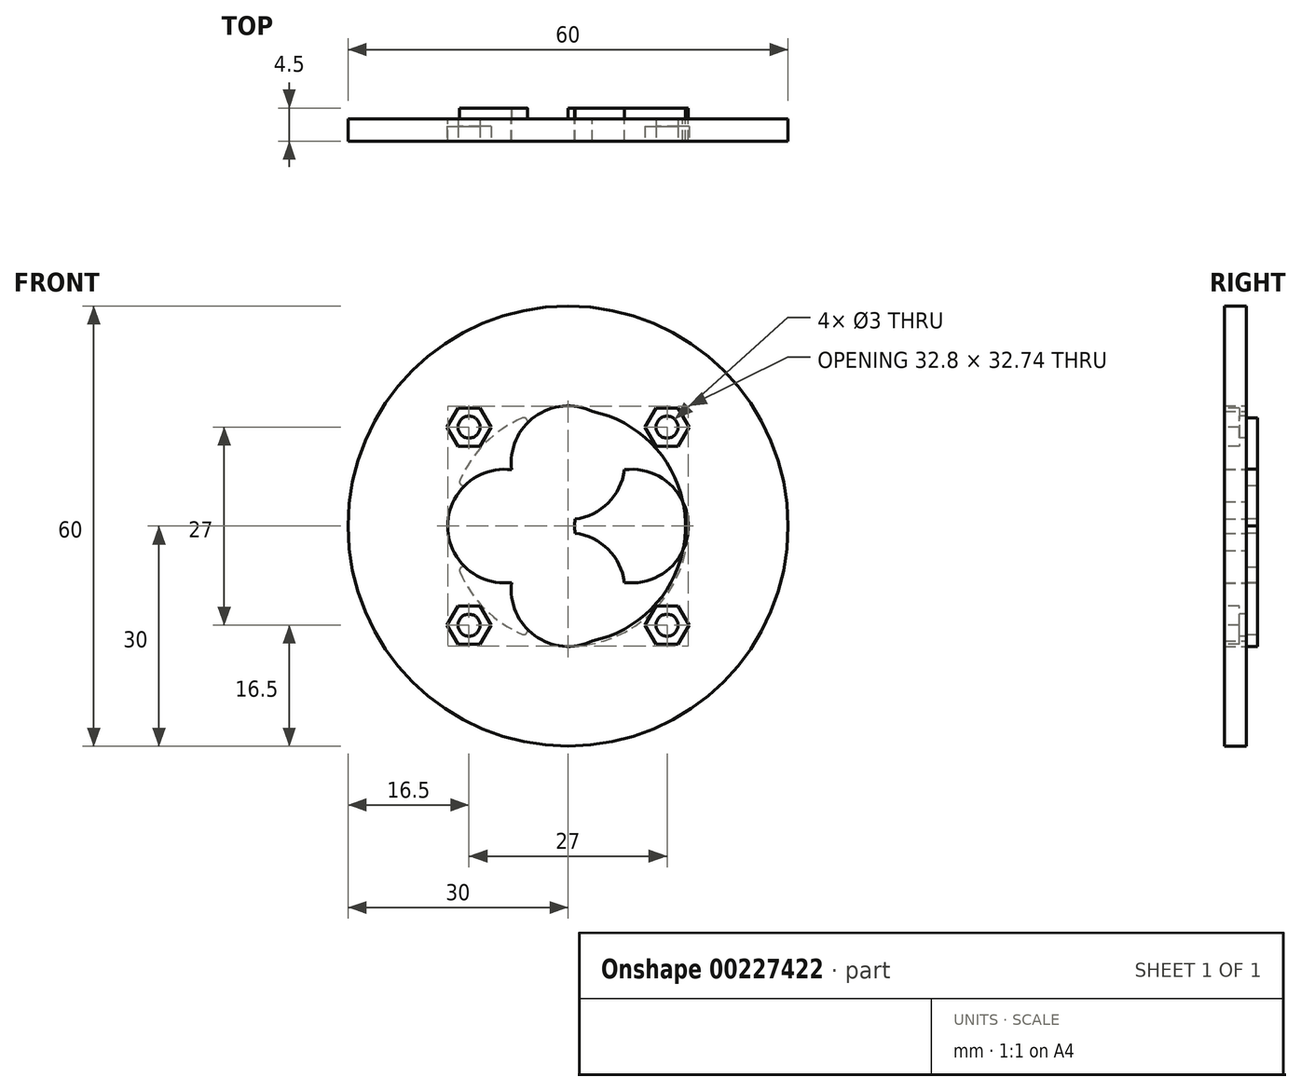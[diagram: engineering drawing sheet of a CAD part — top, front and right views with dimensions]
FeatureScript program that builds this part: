
annotation { "Feature Type Name" : "Feature", "Feature Type Description" : "" }
export const myFeature = defineFeature(function(context is Context, id is Id, definition is map)
    precondition{}
    {
        {
            var Q0;
            Q0=qCreatedBy(makeId("Front.planeOp"),FACE);
            var sketch = newSketch(context, id + "F0", { "sketchPlane" : qUnion([Q0])});
            skCircle(sketch, "E0", {"center": v(0, 0) * mm, "radius": 16.4 * mm});
            skCircle(sketch, "E1", {"center": v(0, -8.65) * mm, "radius": 7.75 * mm});
            skCircle(sketch, "E2", {"center": v(8.65, 0) * mm, "radius": 7.75 * mm});
            skCircle(sketch, "E3", {"center": v(0, 8.65) * mm, "radius": 7.75 * mm});
            skCircle(sketch, "E4", {"center": v(-8.65, 0) * mm, "radius": 7.75 * mm});
            skCircle(sketch, "E5", {"center": v(0, 0) * mm, "radius": 30 * mm});
            skCircle(sketch, "E6", {"center": v(0, 0) * mm, "radius": 16 * mm});
            skSolve(sketch);
        }
        {
            var Q0;
            Q0=makeQuery(id+"F0.imprint","IMPRINT",FACE,{"disambiguationData":[TD([[makeQuery(id+"F0.imprint","IMPRINT",EDGE,{"derivedFrom":sQuery(id+"F0.wireOp",EDGE,"E5")}),1.0]])]});
            var Q1;
            {var subQ0=sQuery(id+"F0.wireOp",EDGE,"E3");var subQ1=sQuery(id+"F0.wireOp",EDGE,"E0");var subQ2=makeQuery(id+"F0.imprint","INTERSECT",VERTEX,{"derivedFrom":[subQ1,subQ0]});Q1=makeQuery(id+"F0.imprint","IMPRINT",FACE,{"disambiguationData":[TD([[makeQuery(id+"F0.imprint","IMPRINT",EDGE,{"disambiguationData":[TD([[subQ2,-1.0]])],"derivedFrom":subQ1}),1.0]])]});}
            var Q2;
            {var subQ0=sQuery(id+"F0.wireOp",EDGE,"E6");var subQ1=sQuery(id+"F0.wireOp",EDGE,"E3");var subQ2=makeQuery(id+"F0.imprint","INTERSECT",VERTEX,{"disambiguationData":[OD(1.0)],"derivedFrom":[subQ1,subQ0]});Q2=makeQuery(id+"F0.imprint","IMPRINT",FACE,{"disambiguationData":[TD([[makeQuery(id+"F0.imprint","IMPRINT",EDGE,{"disambiguationData":[TD([[subQ2,-1.0]])],"derivedFrom":subQ1}),-1.0]])]});}
            var Q3;
            {var subQ0=sQuery(id+"F0.wireOp",EDGE,"E4");var subQ1=sQuery(id+"F0.wireOp",EDGE,"E0");var subQ2=makeQuery(id+"F0.imprint","INTERSECT",VERTEX,{"derivedFrom":[subQ1,subQ0]});Q3=makeQuery(id+"F0.imprint","IMPRINT",FACE,{"disambiguationData":[TD([[makeQuery(id+"F0.imprint","IMPRINT",EDGE,{"disambiguationData":[TD([[subQ2,-1.0]])],"derivedFrom":subQ1}),1.0]])]});}
            var Q4;
            {var subQ0=sQuery(id+"F0.wireOp",EDGE,"E4");var subQ1=sQuery(id+"F0.wireOp",EDGE,"E1");var subQ2=makeQuery(id+"F0.imprint","INTERSECT",VERTEX,{"disambiguationData":[OD(1.0)],"derivedFrom":[subQ1,subQ0]});Q4=makeQuery(id+"F0.imprint","IMPRINT",FACE,{"disambiguationData":[TD([[makeQuery(id+"F0.imprint","IMPRINT",EDGE,{"disambiguationData":[TD([[subQ2,-1.0]])],"derivedFrom":subQ1}),-1.0]])]});}
            var Q5;
            {var subQ0=sQuery(id+"F0.wireOp",EDGE,"E3");var subQ1=sQuery(id+"F0.wireOp",EDGE,"E0");var subQ2=makeQuery(id+"F0.imprint","INTERSECT",VERTEX,{"derivedFrom":[subQ1,subQ0]});Q5=makeQuery(id+"F0.imprint","IMPRINT",FACE,{"disambiguationData":[TD([[makeQuery(id+"F0.imprint","IMPRINT",EDGE,{"disambiguationData":[TD([[subQ2,1.0]])],"derivedFrom":subQ1}),1.0]])]});}
            var Q6;
            {var subQ0=sQuery(id+"F0.wireOp",EDGE,"E6");var subQ1=sQuery(id+"F0.wireOp",EDGE,"E2");var subQ2=makeQuery(id+"F0.imprint","INTERSECT",VERTEX,{"disambiguationData":[OD(0.0)],"derivedFrom":[subQ1,subQ0]});Q6=makeQuery(id+"F0.imprint","IMPRINT",FACE,{"disambiguationData":[TD([[makeQuery(id+"F0.imprint","IMPRINT",EDGE,{"disambiguationData":[TD([[subQ2,-1.0]])],"derivedFrom":subQ1}),-1.0]])]});}
            var Q7;
            {var subQ0=sQuery(id+"F0.wireOp",EDGE,"E2");var subQ1=sQuery(id+"F0.wireOp",EDGE,"E0");var subQ2=makeQuery(id+"F0.imprint","INTERSECT",VERTEX,{"derivedFrom":[subQ1,subQ0]});Q7=makeQuery(id+"F0.imprint","IMPRINT",FACE,{"disambiguationData":[TD([[makeQuery(id+"F0.imprint","IMPRINT",EDGE,{"disambiguationData":[TD([[subQ2,1.0]])],"derivedFrom":subQ1}),1.0]])]});}
            var Q8;
            {var subQ0=sQuery(id+"F0.wireOp",EDGE,"E2");var subQ1=sQuery(id+"F0.wireOp",EDGE,"E1");var subQ2=makeQuery(id+"F0.imprint","INTERSECT",VERTEX,{"disambiguationData":[OD(1.0)],"derivedFrom":[subQ1,subQ0]});Q8=makeQuery(id+"F0.imprint","IMPRINT",FACE,{"disambiguationData":[TD([[makeQuery(id+"F0.imprint","IMPRINT",EDGE,{"disambiguationData":[TD([[subQ2,1.0]])],"derivedFrom":subQ1}),-1.0]])]});}
            extrude(context, id + "F1", {"entities" : qUnion([Q0, Q1, Q2, Q3, Q4, Q5, Q6, Q7, Q8]), "depth" : 3 * mm});
        }
        {
            var Q0;
            {var subQ0=sQuery(id+"F0.wireOp",EDGE,"E6");var subQ1=sQuery(id+"F0.wireOp",EDGE,"E2");var subQ2=makeQuery(id+"F0.imprint","INTERSECT",VERTEX,{"disambiguationData":[OD(0.0)],"derivedFrom":[subQ1,subQ0]});Q0=makeQuery(id+"F0.imprint","IMPRINT",FACE,{"disambiguationData":[TD([[makeQuery(id+"F0.imprint","IMPRINT",EDGE,{"disambiguationData":[TD([[subQ2,-1.0]])],"derivedFrom":subQ1}),-1.0]])]});}
            var Q1;
            {var subQ0=sQuery(id+"F0.wireOp",EDGE,"E2");var subQ1=sQuery(id+"F0.wireOp",EDGE,"E1");var subQ2=makeQuery(id+"F0.imprint","INTERSECT",VERTEX,{"disambiguationData":[OD(1.0)],"derivedFrom":[subQ1,subQ0]});Q1=makeQuery(id+"F0.imprint","IMPRINT",FACE,{"disambiguationData":[TD([[makeQuery(id+"F0.imprint","IMPRINT",EDGE,{"disambiguationData":[TD([[subQ2,1.0]])],"derivedFrom":subQ1}),-1.0]])]});}
            var Q2;
            {var subQ0=sQuery(id+"F0.wireOp",EDGE,"E4");var subQ1=sQuery(id+"F0.wireOp",EDGE,"E1");var subQ2=makeQuery(id+"F0.imprint","INTERSECT",VERTEX,{"disambiguationData":[OD(1.0)],"derivedFrom":[subQ1,subQ0]});Q2=makeQuery(id+"F0.imprint","IMPRINT",FACE,{"disambiguationData":[TD([[makeQuery(id+"F0.imprint","IMPRINT",EDGE,{"disambiguationData":[TD([[subQ2,-1.0]])],"derivedFrom":subQ1}),-1.0]])]});}
            var Q3;
            {var subQ0=sQuery(id+"F0.wireOp",EDGE,"E6");var subQ1=sQuery(id+"F0.wireOp",EDGE,"E3");var subQ2=makeQuery(id+"F0.imprint","INTERSECT",VERTEX,{"disambiguationData":[OD(1.0)],"derivedFrom":[subQ1,subQ0]});Q3=makeQuery(id+"F0.imprint","IMPRINT",FACE,{"disambiguationData":[TD([[makeQuery(id+"F0.imprint","IMPRINT",EDGE,{"disambiguationData":[TD([[subQ2,-1.0]])],"derivedFrom":subQ1}),-1.0]])]});}
            extrude(context, id + "F4", {"entities" : qUnion([Q0, Q1, Q2, Q3]), "oppositeDirection" : true, "depth" : 1.5 * mm});
        }
        {
            var Q0;
            {var subQ0=sQuery(id+"F0.wireOp",EDGE,"E6");var subQ1=sQuery(id+"F0.wireOp",EDGE,"E1");Q0=makeQuery(id+"F4.opExtrude","SWEPT_EDGE",EDGE,{"disambiguationData":[OSD([subQ1,subQ0]),TDD([makeQuery(id+"F0.imprint","INTERSECT",VERTEX,{"disambiguationData":[OD(0.0)],"derivedFrom":[subQ1,subQ0]})])]});}
            var Q1;
            {var subQ0=sQuery(id+"F0.wireOp",EDGE,"E6");var subQ1=sQuery(id+"F0.wireOp",EDGE,"E1");Q1=makeQuery(id+"F4.opExtrude","SWEPT_EDGE",EDGE,{"disambiguationData":[OSD([subQ1,subQ0]),TDD([makeQuery(id+"F0.imprint","INTERSECT",VERTEX,{"disambiguationData":[OD(1.0)],"derivedFrom":[subQ1,subQ0]})])]});}
            var Q2;
            {var subQ0=sQuery(id+"F0.wireOp",EDGE,"E6");var subQ1=sQuery(id+"F0.wireOp",EDGE,"E2");Q2=makeQuery(id+"F4.opExtrude","SWEPT_EDGE",EDGE,{"disambiguationData":[OSD([subQ1,subQ0]),TDD([makeQuery(id+"F0.imprint","INTERSECT",VERTEX,{"disambiguationData":[OD(0.0)],"derivedFrom":[subQ1,subQ0]})])]});}
            var Q3;
            {var subQ0=sQuery(id+"F0.wireOp",EDGE,"E6");var subQ1=sQuery(id+"F0.wireOp",EDGE,"E2");Q3=makeQuery(id+"F4.opExtrude","SWEPT_EDGE",EDGE,{"disambiguationData":[OSD([subQ1,subQ0]),TDD([makeQuery(id+"F0.imprint","INTERSECT",VERTEX,{"disambiguationData":[OD(1.0)],"derivedFrom":[subQ1,subQ0]})])]});}
            var Q4;
            {var subQ0=sQuery(id+"F0.wireOp",EDGE,"E6");var subQ1=sQuery(id+"F0.wireOp",EDGE,"E2");Q4=makeQuery(id+"F4.opExtrude","SWEPT_EDGE",EDGE,{"disambiguationData":[OSD([subQ1,subQ0]),TDD([makeQuery(id+"F0.imprint","INTERSECT",VERTEX,{"disambiguationData":[OD(0.0)],"derivedFrom":[subQ1,subQ0]})])]});}
            var Q5;
            {var subQ0=sQuery(id+"F0.wireOp",EDGE,"E6");var subQ1=sQuery(id+"F0.wireOp",EDGE,"E2");Q5=makeQuery(id+"F4.opExtrude","SWEPT_EDGE",EDGE,{"disambiguationData":[OSD([subQ1,subQ0]),TDD([makeQuery(id+"F0.imprint","INTERSECT",VERTEX,{"disambiguationData":[OD(1.0)],"derivedFrom":[subQ1,subQ0]})])]});}
            var Q6;
            {var subQ0=sQuery(id+"F0.wireOp",EDGE,"E6");var subQ1=sQuery(id+"F0.wireOp",EDGE,"E1");Q6=makeQuery(id+"F4.opExtrude","SWEPT_EDGE",EDGE,{"disambiguationData":[OSD([subQ1,subQ0]),TDD([makeQuery(id+"F0.imprint","INTERSECT",VERTEX,{"disambiguationData":[OD(0.0)],"derivedFrom":[subQ1,subQ0]})])]});}
            var Q7;
            {var subQ0=sQuery(id+"F0.wireOp",EDGE,"E6");var subQ1=sQuery(id+"F0.wireOp",EDGE,"E1");Q7=makeQuery(id+"F4.opExtrude","SWEPT_EDGE",EDGE,{"disambiguationData":[OSD([subQ1,subQ0]),TDD([makeQuery(id+"F0.imprint","INTERSECT",VERTEX,{"disambiguationData":[OD(1.0)],"derivedFrom":[subQ1,subQ0]})])]});}
            var Q8;
            {var subQ0=sQuery(id+"F0.wireOp",EDGE,"E6");var subQ1=sQuery(id+"F0.wireOp",EDGE,"E4");Q8=makeQuery(id+"F4.opExtrude","SWEPT_EDGE",EDGE,{"disambiguationData":[OSD([subQ1,subQ0]),TDD([makeQuery(id+"F0.imprint","INTERSECT",VERTEX,{"disambiguationData":[OD(0.0)],"derivedFrom":[subQ1,subQ0]})])]});}
            var Q9;
            {var subQ0=sQuery(id+"F0.wireOp",EDGE,"E6");var subQ1=sQuery(id+"F0.wireOp",EDGE,"E4");Q9=makeQuery(id+"F4.opExtrude","SWEPT_EDGE",EDGE,{"disambiguationData":[OSD([subQ1,subQ0]),TDD([makeQuery(id+"F0.imprint","INTERSECT",VERTEX,{"disambiguationData":[OD(1.0)],"derivedFrom":[subQ1,subQ0]})])]});}
            var Q10;
            {var subQ0=sQuery(id+"F0.wireOp",EDGE,"E6");var subQ1=sQuery(id+"F0.wireOp",EDGE,"E3");Q10=makeQuery(id+"F4.opExtrude","SWEPT_EDGE",EDGE,{"disambiguationData":[OSD([subQ1,subQ0]),TDD([makeQuery(id+"F0.imprint","INTERSECT",VERTEX,{"disambiguationData":[OD(0.0)],"derivedFrom":[subQ1,subQ0]})])]});}
            var Q11;
            {var subQ0=sQuery(id+"F0.wireOp",EDGE,"E6");var subQ1=sQuery(id+"F0.wireOp",EDGE,"E3");Q11=makeQuery(id+"F4.opExtrude","SWEPT_EDGE",EDGE,{"disambiguationData":[OSD([subQ1,subQ0]),TDD([makeQuery(id+"F0.imprint","INTERSECT",VERTEX,{"disambiguationData":[OD(1.0)],"derivedFrom":[subQ1,subQ0]})])]});}
            var Q12;
            {var subQ0=sQuery(id+"F0.wireOp",EDGE,"E6");var subQ1=sQuery(id+"F0.wireOp",EDGE,"E1");Q12=makeQuery(id+"F4.opExtrude","SWEPT_EDGE",EDGE,{"disambiguationData":[OSD([subQ1,subQ0]),TDD([makeQuery(id+"F0.imprint","INTERSECT",VERTEX,{"disambiguationData":[OD(0.0)],"derivedFrom":[subQ1,subQ0]})])]});}
            var Q13;
            {var subQ0=sQuery(id+"F0.wireOp",EDGE,"E6");var subQ1=sQuery(id+"F0.wireOp",EDGE,"E1");Q13=makeQuery(id+"F4.opExtrude","SWEPT_EDGE",EDGE,{"disambiguationData":[OSD([subQ1,subQ0]),TDD([makeQuery(id+"F0.imprint","INTERSECT",VERTEX,{"disambiguationData":[OD(1.0)],"derivedFrom":[subQ1,subQ0]})])]});}
            var Q14;
            {var subQ0=sQuery(id+"F0.wireOp",EDGE,"E6");var subQ1=sQuery(id+"F0.wireOp",EDGE,"E2");Q14=makeQuery(id+"F4.opExtrude","SWEPT_EDGE",EDGE,{"disambiguationData":[OSD([subQ1,subQ0]),TDD([makeQuery(id+"F0.imprint","INTERSECT",VERTEX,{"disambiguationData":[OD(0.0)],"derivedFrom":[subQ1,subQ0]})])]});}
            var Q15;
            {var subQ0=sQuery(id+"F0.wireOp",EDGE,"E6");var subQ1=sQuery(id+"F0.wireOp",EDGE,"E2");Q15=makeQuery(id+"F4.opExtrude","SWEPT_EDGE",EDGE,{"disambiguationData":[OSD([subQ1,subQ0]),TDD([makeQuery(id+"F0.imprint","INTERSECT",VERTEX,{"disambiguationData":[OD(1.0)],"derivedFrom":[subQ1,subQ0]})])]});}
            var Q16;
            {var subQ0=sQuery(id+"F0.wireOp",EDGE,"E6");var subQ1=sQuery(id+"F0.wireOp",EDGE,"E4");Q16=makeQuery(id+"F4.opExtrude","SWEPT_EDGE",EDGE,{"disambiguationData":[OSD([subQ1,subQ0]),TDD([makeQuery(id+"F0.imprint","INTERSECT",VERTEX,{"disambiguationData":[OD(0.0)],"derivedFrom":[subQ1,subQ0]})])]});}
            var Q17;
            {var subQ0=sQuery(id+"F0.wireOp",EDGE,"E6");var subQ1=sQuery(id+"F0.wireOp",EDGE,"E4");Q17=makeQuery(id+"F4.opExtrude","SWEPT_EDGE",EDGE,{"disambiguationData":[OSD([subQ1,subQ0]),TDD([makeQuery(id+"F0.imprint","INTERSECT",VERTEX,{"disambiguationData":[OD(1.0)],"derivedFrom":[subQ1,subQ0]})])]});}
            var Q18;
            {var subQ0=sQuery(id+"F0.wireOp",EDGE,"E6");var subQ1=sQuery(id+"F0.wireOp",EDGE,"E3");Q18=makeQuery(id+"F4.opExtrude","SWEPT_EDGE",EDGE,{"disambiguationData":[OSD([subQ1,subQ0]),TDD([makeQuery(id+"F0.imprint","INTERSECT",VERTEX,{"disambiguationData":[OD(0.0)],"derivedFrom":[subQ1,subQ0]})])]});}
            var Q19;
            {var subQ0=sQuery(id+"F0.wireOp",EDGE,"E6");var subQ1=sQuery(id+"F0.wireOp",EDGE,"E3");Q19=makeQuery(id+"F4.opExtrude","SWEPT_EDGE",EDGE,{"disambiguationData":[OSD([subQ1,subQ0]),TDD([makeQuery(id+"F0.imprint","INTERSECT",VERTEX,{"disambiguationData":[OD(1.0)],"derivedFrom":[subQ1,subQ0]})])]});}
            var Q20;
            {var subQ0=sQuery(id+"F0.wireOp",EDGE,"E6");var subQ1=sQuery(id+"F0.wireOp",EDGE,"E2");Q20=makeQuery(id+"F4.opExtrude","SWEPT_EDGE",EDGE,{"disambiguationData":[OSD([subQ1,subQ0]),TDD([makeQuery(id+"F0.imprint","INTERSECT",VERTEX,{"disambiguationData":[OD(0.0)],"derivedFrom":[subQ1,subQ0]})])]});}
            var Q21;
            {var subQ0=sQuery(id+"F0.wireOp",EDGE,"E6");var subQ1=sQuery(id+"F0.wireOp",EDGE,"E2");Q21=makeQuery(id+"F4.opExtrude","SWEPT_EDGE",EDGE,{"disambiguationData":[OSD([subQ1,subQ0]),TDD([makeQuery(id+"F0.imprint","INTERSECT",VERTEX,{"disambiguationData":[OD(1.0)],"derivedFrom":[subQ1,subQ0]})])]});}
            fillet(context, id + "F5", {"entities" : qUnion([Q0, Q1, Q2, Q3, Q4, Q5, Q6, Q7, Q8, Q9, Q10, Q11, Q12, Q13, Q14, Q15, Q16, Q17, Q18, Q19, Q20, Q21]), "radius" : 0.5 * mm, "tangentPropagation" : true, "allowEdgeOverflow" : false});
        }
        {
            var Q0;
            Q0=makeQuery(id+"F1.opExtrude","CAP_FACE",FACE,{"disambiguationData":[OSD([sQuery(id+"F0.wireOp",EDGE,"E1"),sQuery(id+"F0.wireOp",EDGE,"E2"),sQuery(id+"F0.wireOp",EDGE,"E3"),sQuery(id+"F0.wireOp",EDGE,"E4"),sQuery(id+"F0.wireOp",EDGE,"E5")])],"isStart":false});
            var sketch = newSketch(context, id + "F2", { "sketchPlane" : qUnion([Q0])});
            skLineSegment(sketch, "E7.bottom", {"start": v(13.5, -13.5) * mm, "end": v(-13.5, -13.5) * mm, "construction": true});
            skLineSegment(sketch, "E7.top", {"start": v(13.5, 13.5) * mm, "end": v(-13.5, 13.5) * mm, "construction": true});
            skLineSegment(sketch, "E7.left", {"start": v(13.5, -13.5) * mm, "end": v(13.5, 13.5) * mm, "construction": true});
            skLineSegment(sketch, "E7.right", {"start": v(-13.5, -13.5) * mm, "end": v(-13.5, 13.5) * mm, "construction": true});
            skPoint(sketch, "E7.middle", {"position": v(0, 0) * mm});
            skCircle(sketch, "E8.cCircle", {"center": v(-13.5, 13.5) * mm, "radius": 2.6 * mm, "construction": true});
            skLineSegment(sketch, "E8.0", {"start": v(-12, 10.9) * mm, "end": v(-15, 10.9) * mm});
            skLineSegment(sketch, "E8.1", {"start": v(-15, 10.9) * mm, "end": v(-16.5, 13.5) * mm});
            skLineSegment(sketch, "E8.2", {"start": v(-16.5, 13.5) * mm, "end": v(-15, 16.1) * mm});
            skLineSegment(sketch, "E8.3", {"start": v(-15, 16.1) * mm, "end": v(-12, 16.1) * mm});
            skLineSegment(sketch, "E8.4", {"start": v(-12, 16.1) * mm, "end": v(-10.5, 13.5) * mm});
            skLineSegment(sketch, "E8.5", {"start": v(-10.5, 13.5) * mm, "end": v(-12, 10.9) * mm});
            skPoint(sketch, "E8.0.midPoint", {"position": v(-13.5, 10.9) * mm});
            skCircle(sketch, "E9.cCircle", {"center": v(13.5, 13.5) * mm, "radius": 2.6 * mm, "construction": true});
            skLineSegment(sketch, "E9.0", {"start": v(15, 10.9) * mm, "end": v(12, 10.9) * mm});
            skLineSegment(sketch, "E9.1", {"start": v(12, 10.9) * mm, "end": v(10.5, 13.5) * mm});
            skLineSegment(sketch, "E9.2", {"start": v(10.5, 13.5) * mm, "end": v(12, 16.1) * mm});
            skLineSegment(sketch, "E9.3", {"start": v(12, 16.1) * mm, "end": v(15, 16.1) * mm});
            skLineSegment(sketch, "E9.4", {"start": v(15, 16.1) * mm, "end": v(16.5, 13.5) * mm});
            skLineSegment(sketch, "E9.5", {"start": v(16.5, 13.5) * mm, "end": v(15, 10.9) * mm});
            skPoint(sketch, "E9.0.midPoint", {"position": v(13.5, 10.9) * mm});
            skCircle(sketch, "E10.cCircle", {"center": v(13.5, -13.5) * mm, "radius": 2.6 * mm, "construction": true});
            skLineSegment(sketch, "E10.0", {"start": v(12, -10.9) * mm, "end": v(15, -10.9) * mm});
            skLineSegment(sketch, "E10.1", {"start": v(15, -10.9) * mm, "end": v(16.5, -13.5) * mm});
            skLineSegment(sketch, "E10.2", {"start": v(16.5, -13.5) * mm, "end": v(15, -16.1) * mm});
            skLineSegment(sketch, "E10.3", {"start": v(15, -16.1) * mm, "end": v(12, -16.1) * mm});
            skLineSegment(sketch, "E10.4", {"start": v(12, -16.1) * mm, "end": v(10.5, -13.5) * mm});
            skLineSegment(sketch, "E10.5", {"start": v(10.5, -13.5) * mm, "end": v(12, -10.9) * mm});
            skPoint(sketch, "E10.0.midPoint", {"position": v(13.5, -10.9) * mm});
            skCircle(sketch, "E11.cCircle", {"center": v(-13.5, -13.5) * mm, "radius": 2.6 * mm, "construction": true});
            skLineSegment(sketch, "E11.0", {"start": v(-15, -10.9) * mm, "end": v(-12, -10.9) * mm});
            skLineSegment(sketch, "E11.1", {"start": v(-12, -10.9) * mm, "end": v(-10.5, -13.5) * mm});
            skLineSegment(sketch, "E11.2", {"start": v(-10.5, -13.5) * mm, "end": v(-12, -16.1) * mm});
            skLineSegment(sketch, "E11.3", {"start": v(-12, -16.1) * mm, "end": v(-15, -16.1) * mm});
            skLineSegment(sketch, "E11.4", {"start": v(-15, -16.1) * mm, "end": v(-16.5, -13.5) * mm});
            skLineSegment(sketch, "E11.5", {"start": v(-16.5, -13.5) * mm, "end": v(-15, -10.9) * mm});
            skPoint(sketch, "E11.0.midPoint", {"position": v(-13.5, -10.9) * mm});
            skCircle(sketch, "E12", {"center": v(-13.5, 13.5) * mm, "radius": 1.5 * mm});
            skCircle(sketch, "E13", {"center": v(13.5, 13.5) * mm, "radius": 1.5 * mm});
            skCircle(sketch, "E14", {"center": v(13.5, -13.5) * mm, "radius": 1.5 * mm});
            skCircle(sketch, "E15", {"center": v(-13.5, -13.5) * mm, "radius": 1.5 * mm});
            skSolve(sketch);
        }
        {
            var Q0;
            Q0=makeQuery(id+"F2.imprint","IMPRINT",FACE,{"disambiguationData":[TD([[makeQuery(id+"F2.imprint","IMPRINT",EDGE,{"derivedFrom":sQuery(id+"F2.wireOp",EDGE,"E8.0")}),-1.0]])]});
            var Q1;
            Q1=makeQuery(id+"F2.imprint","IMPRINT",FACE,{"disambiguationData":[TD([[makeQuery(id+"F2.imprint","IMPRINT",EDGE,{"derivedFrom":sQuery(id+"F2.wireOp",EDGE,"E9.0")}),-1.0]])]});
            var Q2;
            Q2=makeQuery(id+"F2.imprint","IMPRINT",FACE,{"disambiguationData":[TD([[makeQuery(id+"F2.imprint","IMPRINT",EDGE,{"derivedFrom":sQuery(id+"F2.wireOp",EDGE,"E11.0")}),-1.0]])]});
            var Q3;
            Q3=makeQuery(id+"F2.imprint","IMPRINT",FACE,{"disambiguationData":[TD([[makeQuery(id+"F2.imprint","IMPRINT",EDGE,{"derivedFrom":sQuery(id+"F2.wireOp",EDGE,"E10.0")}),-1.0]])]});
            extrude(context, id + "F3", {"entities" : qUnion([Q0, Q1, Q2, Q3]), "operationType" : NewBodyOperationType.REMOVE, "oppositeDirection" : true, "depth" : 2 * mm});
        }
        {
            var Q0;
            Q0=makeQuery(id+"F2.imprint","IMPRINT",FACE,{"disambiguationData":[TD([[makeQuery(id+"F2.imprint","IMPRINT",EDGE,{"derivedFrom":sQuery(id+"F2.wireOp",EDGE,"E12")}),1.0]])]});
            var Q1;
            Q1=makeQuery(id+"F2.imprint","IMPRINT",FACE,{"disambiguationData":[TD([[makeQuery(id+"F2.imprint","IMPRINT",EDGE,{"derivedFrom":sQuery(id+"F2.wireOp",EDGE,"E13")}),1.0]])]});
            var Q2;
            Q2=makeQuery(id+"F2.imprint","IMPRINT",FACE,{"disambiguationData":[TD([[makeQuery(id+"F2.imprint","IMPRINT",EDGE,{"derivedFrom":sQuery(id+"F2.wireOp",EDGE,"E14")}),1.0]])]});
            var Q3;
            Q3=makeQuery(id+"F2.imprint","IMPRINT",FACE,{"disambiguationData":[TD([[makeQuery(id+"F2.imprint","IMPRINT",EDGE,{"derivedFrom":sQuery(id+"F2.wireOp",EDGE,"E15")}),1.0]])]});
            extrude(context, id + "F6", {"entities" : qUnion([Q0, Q1, Q2, Q3]), "operationType" : NewBodyOperationType.REMOVE, "oppositeDirection" : true, "depth" : 25 * mm});
        }
    });
